# Revit family: Haworth_BuzziDesk
name_source: partatom
category: Furniture
revit_build: Autodesk Revit 2018 (Build: 20170223_1515(x64)
units: mm (PartAtom-declared; Revit-internal decimal feet)

## family parameters
Always vertical = Yes
Cut with Voids When Loaded = No
OmniClass Number = 23.40.70.14.64.21
OmniClass Title = Systems Furniture
Room Calculation Point = No
Shared = No
Work Plane-Based = No

## types (3) — shared parameters
Actual Depth = 1 97/256"
Actual Mounting Height = 29 5/8"
Actual Width = 78 3/4"
Assembly Code = E2020200
Custom Size = No
Manufacturer = Haworth
Max. Width = 78 3/4"
Min. Width = 31 1/2"
Model = HCBZ-DKS
Revision Number = 1
Rounded Corners = Yes
Size = Verify Final Dim. w/ Haworth
Squared Corners = No
Standard Widths = 31.5, 39.5, 47.25, 55.25, 63, 71, 78.75 in
URL = http://www.haworth.com
URL - Product = https://www.haworth.com
Void Length = 12"
Warranty = http://www.haworth.com
Width = 78 3/4"

## per-type parameters (varying)
| type | Actual Height | Description | High | Low | Medium |
| HCBZ-DKS1 - Low Screen | 15 3/4" | Haworth BuzziDesk Low Screen | No | Yes | No |
| HCBZ-DKS2 - Medium Screen | 23 3/4" | Haworth BuzziDesk Medium Screen | No | No | Yes |
| HCBZ-DKS3 - High Screen | 31 1/2" | Haworth BuzziDesk High Screen | Yes | No | No |

## geometry (parser evidence)
native form markers: Sweep x3
no freeform markers — native parametric forms only
